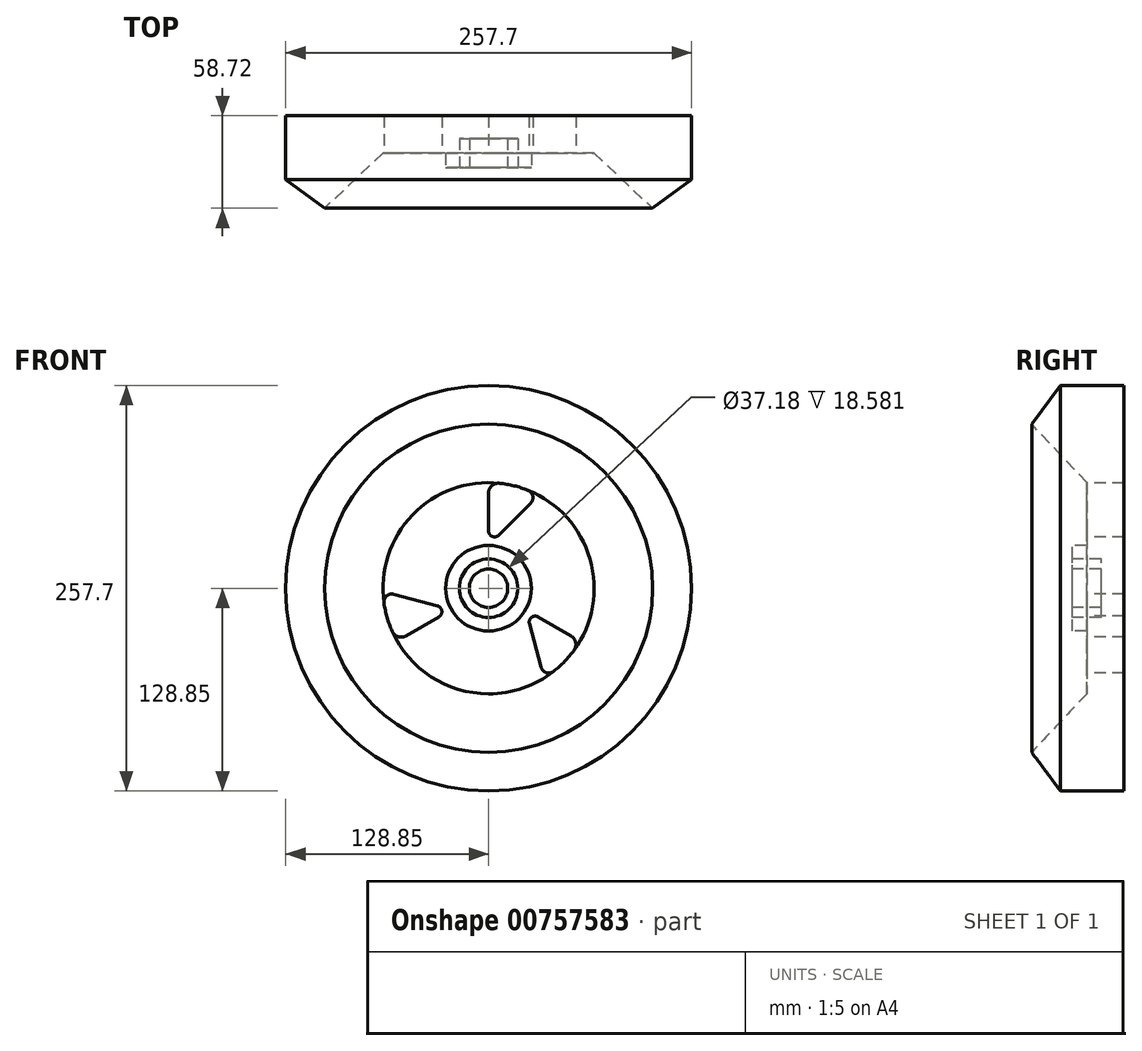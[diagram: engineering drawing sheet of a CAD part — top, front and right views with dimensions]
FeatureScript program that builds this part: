
annotation { "Feature Type Name" : "Feature", "Feature Type Description" : "" }
export const myFeature = defineFeature(function(context is Context, id is Id, definition is map)
    precondition{}
    {
        {
            var Q0;
            Q0=qCreatedBy(makeId("Top.planeOp"),FACE);
            var sketch = newSketch(context, id + "F0", { "sketchPlane" : qUnion([Q0])});
            skLineSegment(sketch, "E0", {"start": v(0, 0) * mm, "end": v(-113.56, 0) * mm});
            skLineSegment(sketch, "E1", {"start": v(-113.56, 0) * mm, "end": v(-113.56, 73.29) * mm});
            skLineSegment(sketch, "E2", {"start": v(-113.56, 73.29) * mm, "end": v(0, 73.29) * mm});
            skLineSegment(sketch, "E3", {"start": v(0, 73.29) * mm, "end": v(0, 0) * mm});
            skSolve(sketch);
        }
        {
            var Q0;
            Q0 = qSketchRegion(id + "F0", true);
            extrude(context, id + "F1", {"entities" : qUnion([Q0]), "depth" : 254 * mm, "offsetDistance" : 25.4 * mm});
        }
        {
            var Q0;
            Q0=makeQuery(id+"F1.opExtrude","SWEPT_FACE",FACE,{"disambiguationData":[OSD([sQuery(id+"F0.wireOp",EDGE,"E3")])]});
            shell(context, id + "F2", {"entities" : qUnion([Q0]), "thickness" : 0.25 * mm});
        }
        {
            var Q0;
            Q0=makeQuery(id+"F1.opExtrude","SWEPT_BODY",BODY,{"disambiguationData":[OSD([sQuery(id+"F0.wireOp",EDGE,"E0"),sQuery(id+"F0.wireOp",EDGE,"E1"),sQuery(id+"F0.wireOp",EDGE,"E2"),sQuery(id+"F0.wireOp",EDGE,"E3")])]});
            deleteBodies(context, id + "F3", {"entities" : qUnion([Q0])});
        }
        {
            var Q0;
            Q0=qCreatedBy(makeId("Top.planeOp"),FACE);
            var sketch = newSketch(context, id + "F4", { "sketchPlane" : qUnion([Q0])});
            skLineSegment(sketch, "E4", {"start": v(0, 0) * mm, "end": v(128.85, 0) * mm});
            skLineSegment(sketch, "E5", {"start": v(128.85, 0) * mm, "end": v(128.85, -40.4) * mm});
            skLineSegment(sketch, "E6", {"start": v(128.85, -40.4) * mm, "end": v(104.21, -58.72) * mm});
            skLineSegment(sketch, "E7", {"start": v(104.21, -58.72) * mm, "end": v(67.05, -23.67) * mm});
            skLineSegment(sketch, "E8", {"start": v(67.05, -23.67) * mm, "end": v(27.2, -23.67) * mm});
            skLineSegment(sketch, "E9", {"start": v(27.2, -23.67) * mm, "end": v(27.2, -32.99) * mm});
            skLineSegment(sketch, "E10", {"start": v(27.2, -32.99) * mm, "end": v(18.6, -32.99) * mm});
            skLineSegment(sketch, "E11", {"start": v(18.6, -32.99) * mm, "end": v(18.6, -14.4) * mm});
            skLineSegment(sketch, "E12", {"start": v(18.6, -14.4) * mm, "end": v(12.18, -14.4) * mm});
            skLineSegment(sketch, "E13", {"start": v(12.18, -14.4) * mm, "end": v(12.18, -32.99) * mm});
            skLineSegment(sketch, "E14", {"start": v(12.18, -32.99) * mm, "end": v(0, -32.99) * mm});
            skLineSegment(sketch, "E15", {"start": v(0, -32.99) * mm, "end": v(0, 0) * mm});
            skSolve(sketch);
        }
        {
            var Q0;
            Q0=makeQuery(id+"F4.imprint","IMPRINT",FACE,{"disambiguationData":[TD([[makeQuery(id+"F4.imprint","IMPRINT",EDGE,{"derivedFrom":sQuery(id+"F4.wireOp",EDGE,"E4")}),-1.0]])]});
            var Q1;
            Q1=sQuery(id+"F4.wireOp",EDGE,"E15");
            revolve(context, id + "F5", {"surfaceOperationType" : NewSurfaceOperationType.NEW, "entities" : qUnion([Q0]), "axis" : qUnion([Q1]), "revolveType" : RevolveType.FULL});
        }
        {
            var Q0;
            Q0=makeQuery(id+"F5.opRevolve","SWEPT_FACE",FACE,{"disambiguationData":[OSD([sQuery(id+"F4.wireOp",EDGE,"E8")])]});
            var sketch = newSketch(context, id + "F6", { "sketchPlane" : qUnion([Q0])});
            skArc(sketch, "E16.0", {"start": v(25, 62.22) * mm, "mid": v(16.16, 65.08) * mm, "end": v(7.01, 66.69) * mm});
            skArc(sketch, "E17.0.0", {"start": v(31.82, 59.03) * mm, "mid": v(16.4, 65.02) * mm, "end": v(0, 67.05) * mm});
            skCircle(sketch, "E18.0", {"center": v(0, 0) * mm, "radius": 12.18 * mm});
            skLineSegment(sketch, "E19", {"start": v(0, 36.4) * mm, "end": v(0, 60.37) * mm});
            skLineSegment(sketch, "E20", {"start": v(6.5, 33.71) * mm, "end": v(26.7, 53.91) * mm});
            skPoint(sketch, "E21.visualSharp", {"position": v(0, 67.05) * mm});
            skArc(sketch, "E21.filletArc", {"start": v(7.01, 66.69) * mm, "mid": v(2.1, 65.09) * mm, "end": v(0, 60.37) * mm});
            skPoint(sketch, "E22.visualSharp", {"position": v(31.82, 59.03) * mm});
            skArc(sketch, "E22.filletArc", {"start": v(26.7, 53.91) * mm, "mid": v(28.09, 58.52) * mm, "end": v(25, 62.22) * mm});
            skPoint(sketch, "E23.visualSharp", {"position": v(0, 27.2) * mm});
            skArc(sketch, "E23.filletArc", {"start": v(0, 36.4) * mm, "mid": v(2.35, 32.89) * mm, "end": v(6.5, 33.71) * mm});
            skLineSegment(sketch, "E24.1.0", {"start": v(25.94, -22.49) * mm, "end": v(33.34, -50.08) * mm});
            skArc(sketch, "E24.1.1", {"start": v(31.53, -18.2) * mm, "mid": v(27.3, -18.48) * mm, "end": v(25.94, -22.49) * mm});
            skLineSegment(sketch, "E24.1.2", {"start": v(31.53, -18.2) * mm, "end": v(52.28, -30.19) * mm});
            skArc(sketch, "E24.1.3", {"start": v(54.24, -39.42) * mm, "mid": v(55.32, -34.36) * mm, "end": v(52.28, -30.19) * mm});
            skArc(sketch, "E24.1.4", {"start": v(41.38, -52.76) * mm, "mid": v(48.28, -46.54) * mm, "end": v(54.24, -39.42) * mm});
            skArc(sketch, "E24.1.5", {"start": v(33.34, -50.08) * mm, "mid": v(36.64, -53.58) * mm, "end": v(41.38, -52.76) * mm});
            skLineSegment(sketch, "E24.2.0", {"start": v(-32.45, -11.22) * mm, "end": v(-60.04, -3.83) * mm});
            skArc(sketch, "E24.2.1", {"start": v(-31.53, -18.2) * mm, "mid": v(-29.66, -14.4) * mm, "end": v(-32.45, -11.22) * mm});
            skLineSegment(sketch, "E24.2.2", {"start": v(-31.53, -18.2) * mm, "end": v(-52.28, -30.19) * mm});
            skArc(sketch, "E24.2.3", {"start": v(-61.26, -27.27) * mm, "mid": v(-57.42, -30.73) * mm, "end": v(-52.28, -30.19) * mm});
            skArc(sketch, "E24.2.4", {"start": v(-66.38, -9.45) * mm, "mid": v(-64.44, -18.54) * mm, "end": v(-61.26, -27.27) * mm});
            skArc(sketch, "E24.2.5", {"start": v(-60.04, -3.83) * mm, "mid": v(-64.72, -4.94) * mm, "end": v(-66.38, -9.45) * mm});
            skLineSegment(sketch, "E24.anchor1", {"start": v(0, 0) * mm, "end": v(6.5, 33.71) * mm, "construction": true});
            skLineSegment(sketch, "E24.anchor2", {"start": v(0, 0) * mm, "end": v(-32.45, -11.22) * mm, "construction": true});
            skSolve(sketch);
        }
        {
            var Q0;
            Q0=makeQuery(id+"F6.imprint","IMPRINT",FACE,{"disambiguationData":[TD([[makeQuery(id+"F6.imprint","IMPRINT",EDGE,{"derivedFrom":sQuery(id+"F6.wireOp",EDGE,"E19")}),-1.0]])]});
            var Q1;
            Q1=makeQuery(id+"F6.imprint","IMPRINT",FACE,{"disambiguationData":[TD([[makeQuery(id+"F6.imprint","IMPRINT",EDGE,{"derivedFrom":sQuery(id+"F6.wireOp",EDGE,"E24.1.0")}),1.0]])]});
            var Q2;
            Q2=makeQuery(id+"F6.imprint","IMPRINT",FACE,{"disambiguationData":[TD([[makeQuery(id+"F6.imprint","IMPRINT",EDGE,{"derivedFrom":sQuery(id+"F6.wireOp",EDGE,"E24.2.0")}),1.0]])]});
            extrude(context, id + "F7", {"entities" : qUnion([Q0, Q1, Q2]), "operationType" : NewBodyOperationType.REMOVE, "endBound" : BoundingType.UP_TO_NEXT, "oppositeDirection" : true, "depth" : 25.4 * mm, "offsetDistance" : 25.4 * mm});
        }
    });
